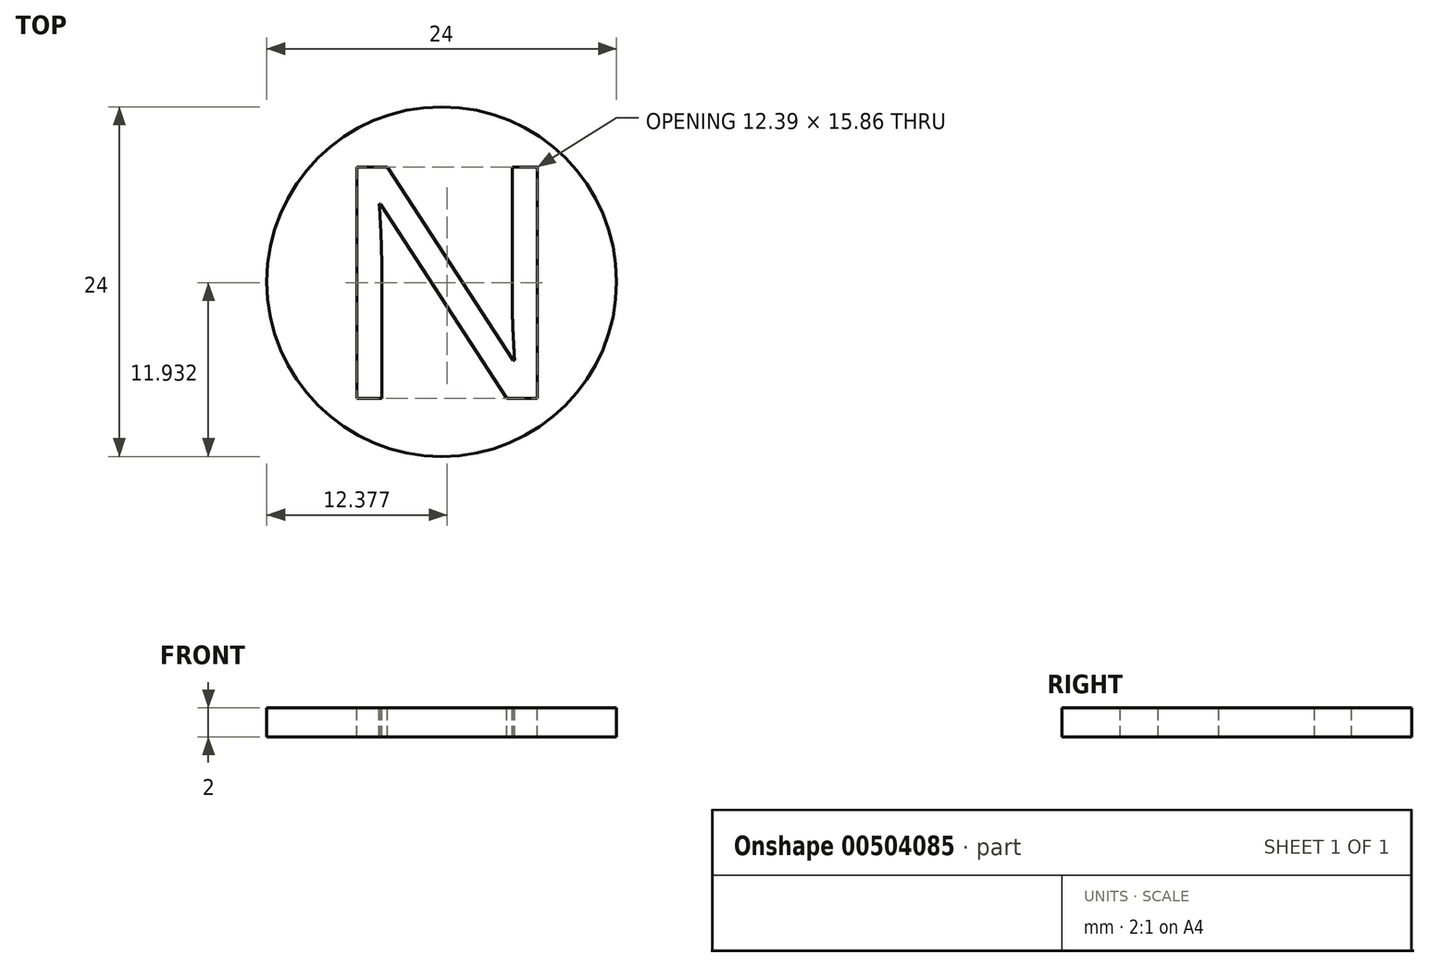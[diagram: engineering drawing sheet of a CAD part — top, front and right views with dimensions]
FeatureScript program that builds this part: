
annotation { "Feature Type Name" : "Feature", "Feature Type Description" : "" }
export const myFeature = defineFeature(function(context is Context, id is Id, definition is map)
    precondition{}
    {
        {
            var Q0;
            Q0=qCreatedBy(makeId("Top.planeOp"),FACE);
            var sketch = newSketch(context, id + "F0", { "sketchPlane" : qUnion([Q0])});
            skCircle(sketch, "E0", {"center": v(0, 0) * mm, "radius": 12 * mm});
            skSolve(sketch);
        }
        {
            var Q0;
            Q0=qSketchRegion(id+"F0",true);
            extrude(context, id + "F1", {"entities" : qUnion([Q0]), "depth" : 2 * mm});
        }
        {
            var Q0;
            Q0=makeQuery(id+"F1.opExtrude","CAP_FACE",FACE,{"disambiguationData":[OSD([sQuery(id+"F0.wireOp",EDGE,"E0")])],"isStart":false});
            var sketch = newSketch(context, id + "F2", { "sketchPlane" : qUnion([Q0])});
            skText(sketch, "E1", { "text": "N", "fontName": "OpenSans-Regular.ttf"});
            skPoint(sketch, "E2", {"position": v(8, 0) * mm});
            const initialGuessF2  = {"E1": [-0.008, -0.008, 1, 0, 0.016]};
            skSetInitialGuess(sketch, initialGuessF2);
            skSolve(sketch);
        }
        {
            var Q0;
            Q0 = qSketchRegion(id + "F2", true);
            extrude(context, id + "F3", {"entities" : qUnion([Q0]), "operationType" : NewBodyOperationType.REMOVE, "oppositeDirection" : true, "depth" : 25 * mm, "offsetDistance" : 25 * mm});
        }
    });
